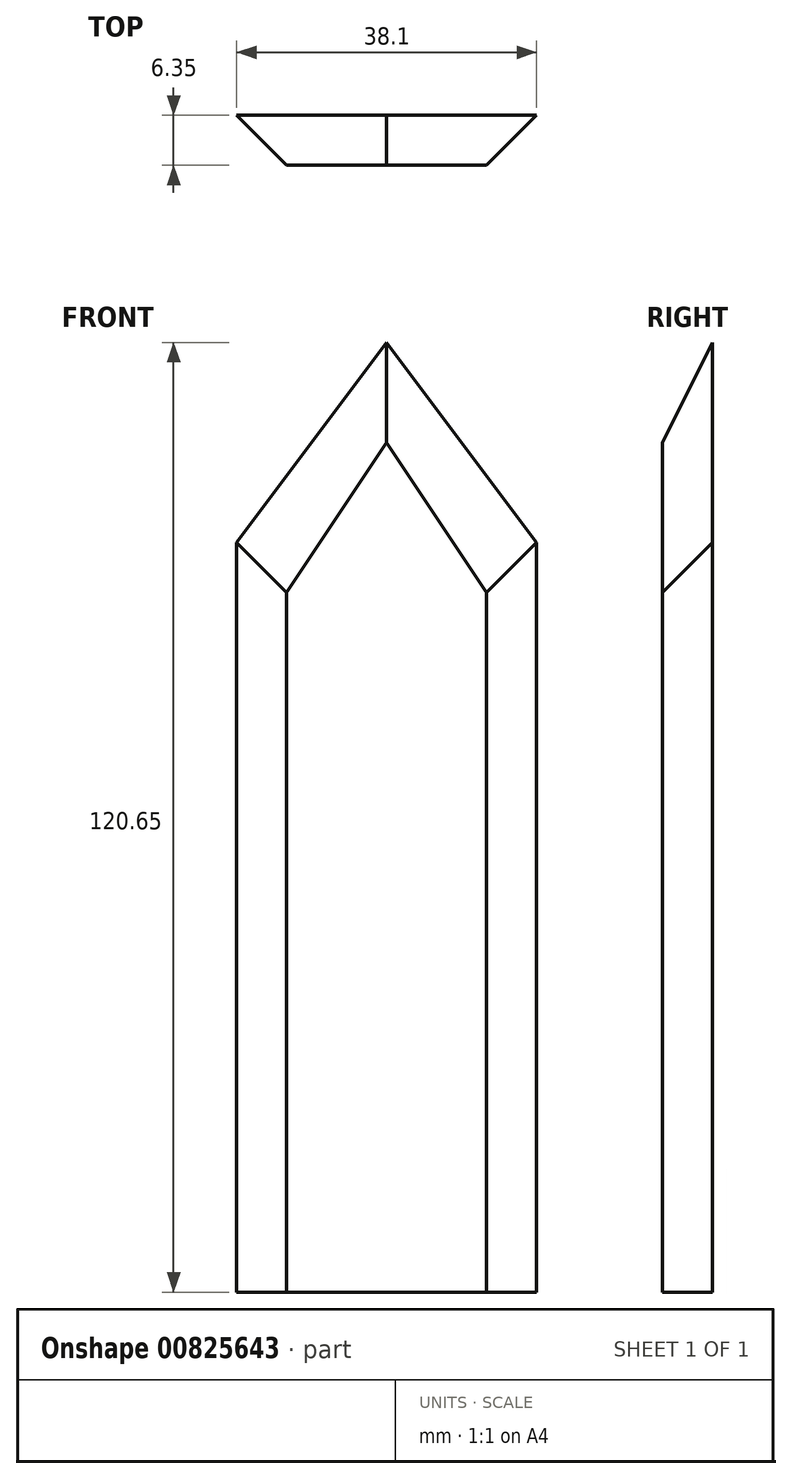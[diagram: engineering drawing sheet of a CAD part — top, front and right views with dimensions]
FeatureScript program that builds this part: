
annotation { "Feature Type Name" : "Feature", "Feature Type Description" : "" }
export const myFeature = defineFeature(function(context is Context, id is Id, definition is map)
    precondition{}
    {
        {
            var Q0;
            Q0=qCreatedBy(makeId("Front.planeOp"),FACE);
            var sketch = newSketch(context, id + "F0", { "sketchPlane" : qUnion([Q0])});
            skLineSegment(sketch, "E0", {"start": v(0, 0) * mm, "end": v(-19.05, 0) * mm});
            skLineSegment(sketch, "E1", {"start": v(-19.05, 0) * mm, "end": v(-19.05, 82.55) * mm});
            skLineSegment(sketch, "E2", {"start": v(-19.05, 82.55) * mm, "end": v(0, 107.95) * mm});
            skLineSegment(sketch, "E3.MirrorCS", {"start": v(19.05, 82.55) * mm, "end": v(0, 107.95) * mm});
            skLineSegment(sketch, "E4.MirrorCS", {"start": v(19.05, 0) * mm, "end": v(19.05, 82.55) * mm});
            skLineSegment(sketch, "E5.MirrorCS", {"start": v(0, 0) * mm, "end": v(19.05, 0) * mm});
            skSolve(sketch);
        }
        {
            var Q0;
            {var subQ3=sQuery(id+"F0.wireOp",EDGE,"E0");Q0=makeQuery(id+"F0.imprint","IMPRINT",FACE,{"disambiguationData":[TD([[makeQuery(id+"F0.imprint","IMPRINT",EDGE,{"derivedFrom":subQ3}),-1.0]])]});}
            cPlane(context, id + "F1", {"entities" : qUnion([Q0]), "cplaneType" : CPlaneType.OFFSET, "offset" : 6.35 * mm, "width" : 152.4 * mm, "height" : 152.4 * mm});
        }
        {
            var Q0;
            Q0=qCreatedBy(id+"F1.planeOp",FACE);
            var sketch = newSketch(context, id + "F2", { "sketchPlane" : qUnion([Q0])});
            skLineSegment(sketch, "E6", {"start": v(0, 0) * mm, "end": v(-12.7, 0) * mm});
            skLineSegment(sketch, "E7", {"start": v(-12.7, 0) * mm, "end": v(-12.7, 76.2) * mm});
            skLineSegment(sketch, "E8", {"start": v(-12.7, 76.2) * mm, "end": v(0, 95.25) * mm});
            skLineSegment(sketch, "E9.MirrorCS", {"start": v(12.7, 76.2) * mm, "end": v(0, 95.25) * mm});
            skLineSegment(sketch, "E10", {"start": v(0, 76.2) * mm, "end": v(0, 95.25) * mm});
            skLineSegment(sketch, "E11.MirrorCS", {"start": v(12.7, 0) * mm, "end": v(12.7, 76.2) * mm});
            skLineSegment(sketch, "E12.MirrorCS", {"start": v(0, 0) * mm, "end": v(12.7, 0) * mm});
            skSolve(sketch);
        }
        {
            var Q0;
            Q0=makeQuery(id+"F0.imprint","IMPRINT",FACE,{"disambiguationData":[TD([[makeQuery(id+"F0.imprint","IMPRINT",EDGE,{"derivedFrom":sQuery(id+"F0.wireOp",EDGE,"E0")}),-1.0]])]});
            var Q1;
            Q1=makeQuery(id+"F2.imprint","IMPRINT",FACE,{"disambiguationData":[TD([[makeQuery(id+"F2.imprint","IMPRINT",EDGE,{"derivedFrom":sQuery(id+"F2.wireOp",EDGE,"E6")}),-1.0]])]});
            loft(context, id + "F3", {"sheetProfilesArray" : [{ "sheetProfileEntities" : qUnion([Q0]) }, { "sheetProfileEntities" : qUnion([Q1]) }]});
        }
        {
            var Q0;
            Q0=makeQuery(id+"F3.opLoft","SWEPT_FACE",FACE,{"disambiguationData":[OSD([sQuery(id+"F0.wireOp",EDGE,"E0"),sQuery(id+"F0.wireOp",EDGE,"E1"),sQuery(id+"F0.wireOp",EDGE,"E5.MirrorCS"),sQuery(id+"F2.wireOp",EDGE,"E6"),sQuery(id+"F2.wireOp",EDGE,"E7"),sQuery(id+"F2.wireOp",EDGE,"E12.MirrorCS")])]});
            var sketch = newSketch(context, id + "F4", { "sketchPlane" : qUnion([Q0])});
            skLineSegment(sketch, "E13", {"start": v(0, 0) * mm, "end": v(-1.04, 0) * mm});
            skLineSegment(sketch, "E14", {"start": v(0, 0) * mm, "end": v(-19.05, 0) * mm});
            skSolve(sketch);
        }
        {
            var Q0;
            {var subQ0=sQuery(id+"F2.wireOp",EDGE,"E12.MirrorCS");var subQ3=sQuery(id+"F2.wireOp",EDGE,"E7");var subQ4=sQuery(id+"F2.wireOp",EDGE,"E6");Q0=makeQuery(id+"F4.imprint","IMPRINT",FACE,{"disambiguationData":[TD([[makeQuery(id+"F4.imprint","IMPRINT",EDGE,{"derivedFrom":makeQuery(id+"F3.opLoft","MID_CAP_EDGE",EDGE,{"disambiguationData":[OSD([subQ4,subQ3,subQ0])],"capPos":1.0})}),-1.0]])]});}
            extrude(context, id + "F5", {"entities" : qUnion([Q0]), "operationType" : NewBodyOperationType.ADD, "depth" : 12.7 * mm, "offsetDistance" : 25.4 * mm});
        }
    });
